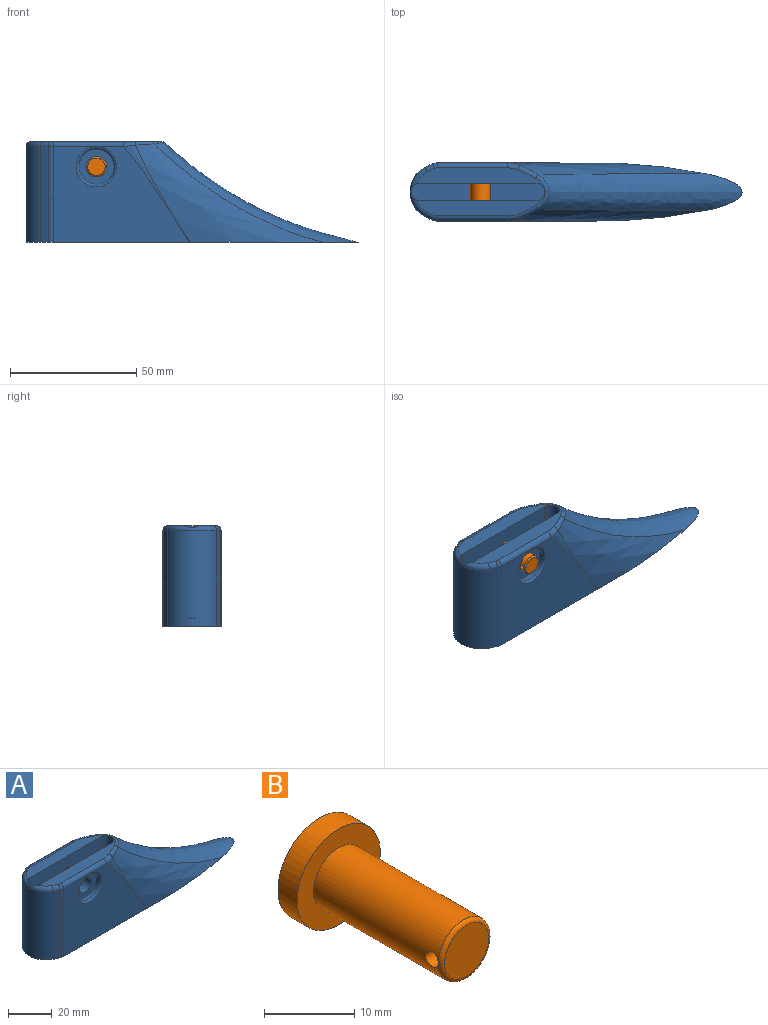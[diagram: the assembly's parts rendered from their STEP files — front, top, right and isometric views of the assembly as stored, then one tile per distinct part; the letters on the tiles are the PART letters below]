
ASSEMBLY  parts=2 mates=1
PART A: 41 faces, bbox 147x25.1x52.8 mm
  f0: plane 51x19mm, normal (0,0,1), area 508.2mm2, adj f14,f15,f16,f17,f24,f25,f26,f27
  f1: cylinder r=4mm len=8mm, axis (0,-1,0), area 125.7mm2, adj f13,f15
  f2: plane 131.51x23.41mm, normal (0,0,-1), area 2663.9mm2, adj f3,f4,f5,f6,f7,f8,f20,f22
  f3: bspline ~105x40mm, area 966.5mm2, adj f2,f21,f22,f28,f35
  f4: plane 53.92x38.04mm, normal (0,-1,0), area 1380.1mm2, adj f2,f21,f22,f24,f34,f39
  f5: cylinder r=31mm len=38mm, axis (0,0,1), area 129.7mm2, adj f2,f23,f25,f39
  f6: cylinder r=31mm len=38mm, axis (0,0,1), area 129.7mm2, adj f2,f23,f29,f37
  f7: plane 55.12x39.23mm, normal (0,1,0), area 1380.1mm2, adj f2,f19,f20,f31,f33,f37
  f8: bspline ~105x40mm, area 966.6mm2, adj f2,f19,f20,f30,f35
  f9: cylinder r=4mm len=8mm, axis (0,-1,0), area 125.7mm2, adj f11,f14
  f10: cylinder r=7mm len=14mm, axis (0,-1,0), area 88mm2, adj f11,f34
  f11: plane 14x14mm, normal (0,-1,0), area 103.7mm2, adj f9,f10
  f12: cylinder r=7mm len=14mm, axis (0,1,0), area 88mm2, adj f13,f33
  f13: plane 14x14mm, normal (0,1,0), area 103.7mm2, adj f1,f12
  f14: plane 46x37mm, normal (0,1,0), area 1651.7mm2, adj f0,f9,f16,f17,f18
  f15: plane 46x37mm, normal (0,-1,0), area 1651.7mm2, adj f0,f1,f16,f17,f18
  f16: cylinder r=3.5mm len=37mm, axis (0,0,1), area 403.4mm2, adj f0,f14,f15,f18,f27
  f17: cylinder r=3.5mm len=37mm, axis (0,0,1), area 406.8mm2, adj f0,f14,f15,f18
  f18: plane 53x7mm, normal (0,0,1), area 360.5mm2, adj f14,f15,f16,f17
  f19: bspline ~33.47x21.72mm, area 34.2mm2, adj f7,f8,f32
  f20: bspline ~13.53x8.57mm, area 1.4mm2, adj f2,f7,f8
  f21: bspline ~33.47x21.72mm, area 36.9mm2, adj f3,f4,f26
  f22: bspline ~13.53x8.57mm, area 1.4mm2, adj f2,f3,f4
  f23: cylinder r=11mm len=38mm, axis (0,0,-1), area 906.6mm2, adj f2,f5,f6,f27
  f24: cylinder r=2mm len=27.83mm, axis (1,0,0), area 87.4mm2, adj f0,f4,f26,f40
  f25: torus R=29mm, axis (0,0,1), area 10.5mm2, adj f0,f5,f27,f40
  f26: bspline ~7.4x3.3mm, area 13.3mm2, adj f0,f21,f24,f28
  f27: torus R=9mm, axis (0,0,1), area 61.3mm2, adj f0,f16,f23,f25,f29
  f28: bspline ~12.65x7.67mm, area 18.5mm2, adj f0,f3,f26,f36
  f29: torus R=29mm, axis (0,0,1), area 10.5mm2, adj f0,f6,f27,f38
  f30: bspline ~11.11x6.77mm, area 18.5mm2, adj f0,f8,f32,f36
  f31: cylinder r=2mm len=27.83mm, axis (1,0,0), area 87.4mm2, adj f0,f7,f32,f38
  f32: bspline ~6.29x3.19mm, area 13.3mm2, adj f0,f19,f30,f31
  f33: torus R=8mm, axis (0,1,0), area 72.7mm2, adj f7,f12
  f34: torus R=8mm, axis (0,1,0), area 72.7mm2, adj f4,f10
  f35: bspline ~88.34x51.56mm, area 1417.1mm2, adj f2,f3,f8,f36
  f36: bspline ~15.44x6.59mm, area 27.5mm2, adj f0,f28,f30,f35
  f37: cylinder r=5mm len=38mm, axis (0,0,1), area 71.5mm2, adj f2,f6,f7,f38
  f38: torus R=3mm, axis (0,0,1), area 5.1mm2, adj f0,f29,f31,f37
  f39: cylinder r=5mm len=38mm, axis (0,0,1), area 71.5mm2, adj f2,f4,f5,f40
  f40: torus R=3mm, axis (0,0,1), area 5.1mm2, adj f0,f24,f25,f39
PART B: 7 faces, bbox 13x23x13 mm
  f0: cylinder r=6.5mm len=13mm, axis (0,1,0), area 122.5mm2, adj f1,f2
  f1: plane 13x13mm, normal (0,-1,0), area 83.7mm2, adj f0,f3
  f2: plane 13x13mm, normal (0,1,0), area 132.7mm2, adj f0
  f3: cylinder r=3.95mm len=19.5mm, axis (0,1,0), area 477.6mm2, adj f1,f5,f6
  f4: plane 6.9x6.9mm, normal (0,-1,0), area 37.4mm2, adj f6
  f5: cylinder r=1mm len=7.9mm, axis (1,0,0), area 48.8mm2, adj f3
  f6: torus R=3.45mm, axis (0,-1,0), area 18.6mm2, adj f3,f4
PLACE A t=(30.86,17.99,-0.55)mm
PLACE B t=(-11.14,29.49,29.45)mm
MATE fastened B.f0 <-> A.f12  axis (0,-1,0) through (-11.14,26.49,29.45)mm
